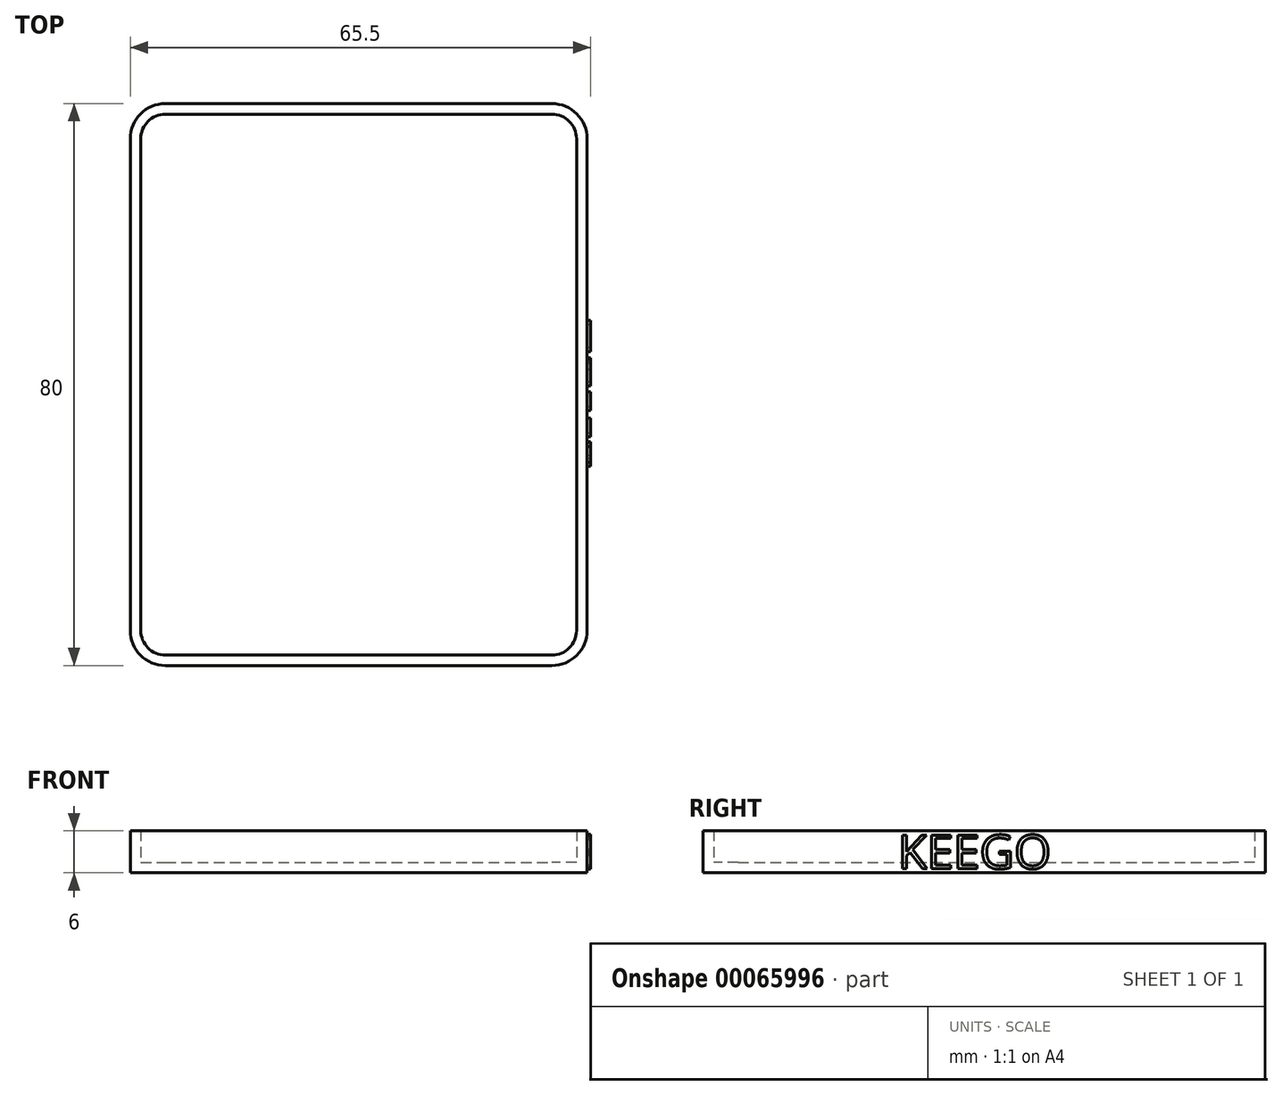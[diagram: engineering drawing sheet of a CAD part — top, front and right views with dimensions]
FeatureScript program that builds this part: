
annotation { "Feature Type Name" : "Feature", "Feature Type Description" : "" }
export const myFeature = defineFeature(function(context is Context, id is Id, definition is map)
    precondition{}
    {
        {
            var Q0;
            Q0=qCreatedBy(makeId("Top.planeOp"),FACE);
            var sketch = newSketch(context, id + "F0", { "sketchPlane" : qUnion([Q0])});
            skLineSegment(sketch, "E0.bottom", {"start": v(-24.54, -21.1) * mm, "end": v(30.46, -21.1) * mm});
            skLineSegment(sketch, "E0.top", {"start": v(-24.54, 58.9) * mm, "end": v(30.46, 58.9) * mm});
            skLineSegment(sketch, "E0.left", {"start": v(-29.54, -16.1) * mm, "end": v(-29.54, 53.9) * mm});
            skLineSegment(sketch, "E0.right", {"start": v(35.46, -16.1) * mm, "end": v(35.46, 53.9) * mm});
            skPoint(sketch, "E1.visualSharp", {"position": v(-29.54, 58.9) * mm});
            skArc(sketch, "E1.filletArc", {"start": v(-24.54, 58.9) * mm, "mid": v(-28.08, 57.43) * mm, "end": v(-29.54, 53.9) * mm});
            skPoint(sketch, "E2.visualSharp", {"position": v(-29.54, -21.1) * mm});
            skArc(sketch, "E2.filletArc", {"start": v(-29.54, -16.1) * mm, "mid": v(-28.08, -19.65) * mm, "end": v(-24.54, -21.1) * mm});
            skPoint(sketch, "E3.visualSharp", {"position": v(35.46, 58.9) * mm});
            skArc(sketch, "E3.filletArc", {"start": v(35.46, 53.9) * mm, "mid": v(34, 57.43) * mm, "end": v(30.46, 58.9) * mm});
            skPoint(sketch, "E4.visualSharp", {"position": v(35.46, -21.1) * mm});
            skArc(sketch, "E4.filletArc", {"start": v(30.46, -21.1) * mm, "mid": v(34, -19.65) * mm, "end": v(35.46, -16.1) * mm});
            skArc(sketch, "E5.0", {"start": v(-28.04, -16.1) * mm, "mid": v(-27.02, -18.58) * mm, "end": v(-24.54, -19.6) * mm});
            skLineSegment(sketch, "E5.1", {"start": v(-24.54, -19.6) * mm, "end": v(30.46, -19.6) * mm});
            skLineSegment(sketch, "E5.2", {"start": v(-28.04, -16.1) * mm, "end": v(-28.04, 53.9) * mm});
            skArc(sketch, "E5.3", {"start": v(30.46, -19.6) * mm, "mid": v(32.93, -18.58) * mm, "end": v(33.96, -16.1) * mm});
            skArc(sketch, "E5.4", {"start": v(-24.54, 57.4) * mm, "mid": v(-27.02, 56.37) * mm, "end": v(-28.04, 53.9) * mm});
            skLineSegment(sketch, "E5.5", {"start": v(-24.54, 57.4) * mm, "end": v(30.46, 57.4) * mm});
            skArc(sketch, "E5.6", {"start": v(33.96, 53.9) * mm, "mid": v(32.93, 56.37) * mm, "end": v(30.46, 57.4) * mm});
            skLineSegment(sketch, "E5.7", {"start": v(33.96, -16.1) * mm, "end": v(33.96, 53.9) * mm});
            skSolve(sketch);
        }
        {
            var Q0;
            Q0=makeQuery(id+"F0.imprint","IMPRINT",FACE,{"disambiguationData":[TD([[makeQuery(id+"F0.imprint","IMPRINT",EDGE,{"derivedFrom":sQuery(id+"F0.wireOp",EDGE,"E5.0")}),1.0]])]});
            extrude(context, id + "F1", {"entities" : qUnion([Q0]), "depth" : 1.5 * mm});
        }
        {
            var Q0;
            Q0 = qSketchRegion(id + "F0", true);
            extrude(context, id + "F2", {"entities" : qUnion([Q0]), "operationType" : NewBodyOperationType.ADD, "depth" : 6 * mm});
        }
        {
            var Q0;
            Q0=makeQuery(id+"F2.opExtrude","SWEPT_FACE",FACE,{"disambiguationData":[OSD([sQuery(id+"F0.wireOp",EDGE,"E0.right")])]});
            var sketch = newSketch(context, id + "F3", { "sketchPlane" : qUnion([Q0])});
            skText(sketch, "E6", { "text": "KEEGO", "fontName": "OpenSans-Regular.ttf"});
            const initialGuessF3  = {"E6": [0.00663, 0.00058, 1, 0, 0.00485]};
            skSetInitialGuess(sketch, initialGuessF3);
            skSolve(sketch);
        }
        {
            var Q0;
            Q0 = qSketchRegion(id + "F3", true);
            extrude(context, id + "F4", {"entities" : qUnion([Q0]), "operationType" : NewBodyOperationType.ADD, "depth" : .5 * mm});
        }
    });
